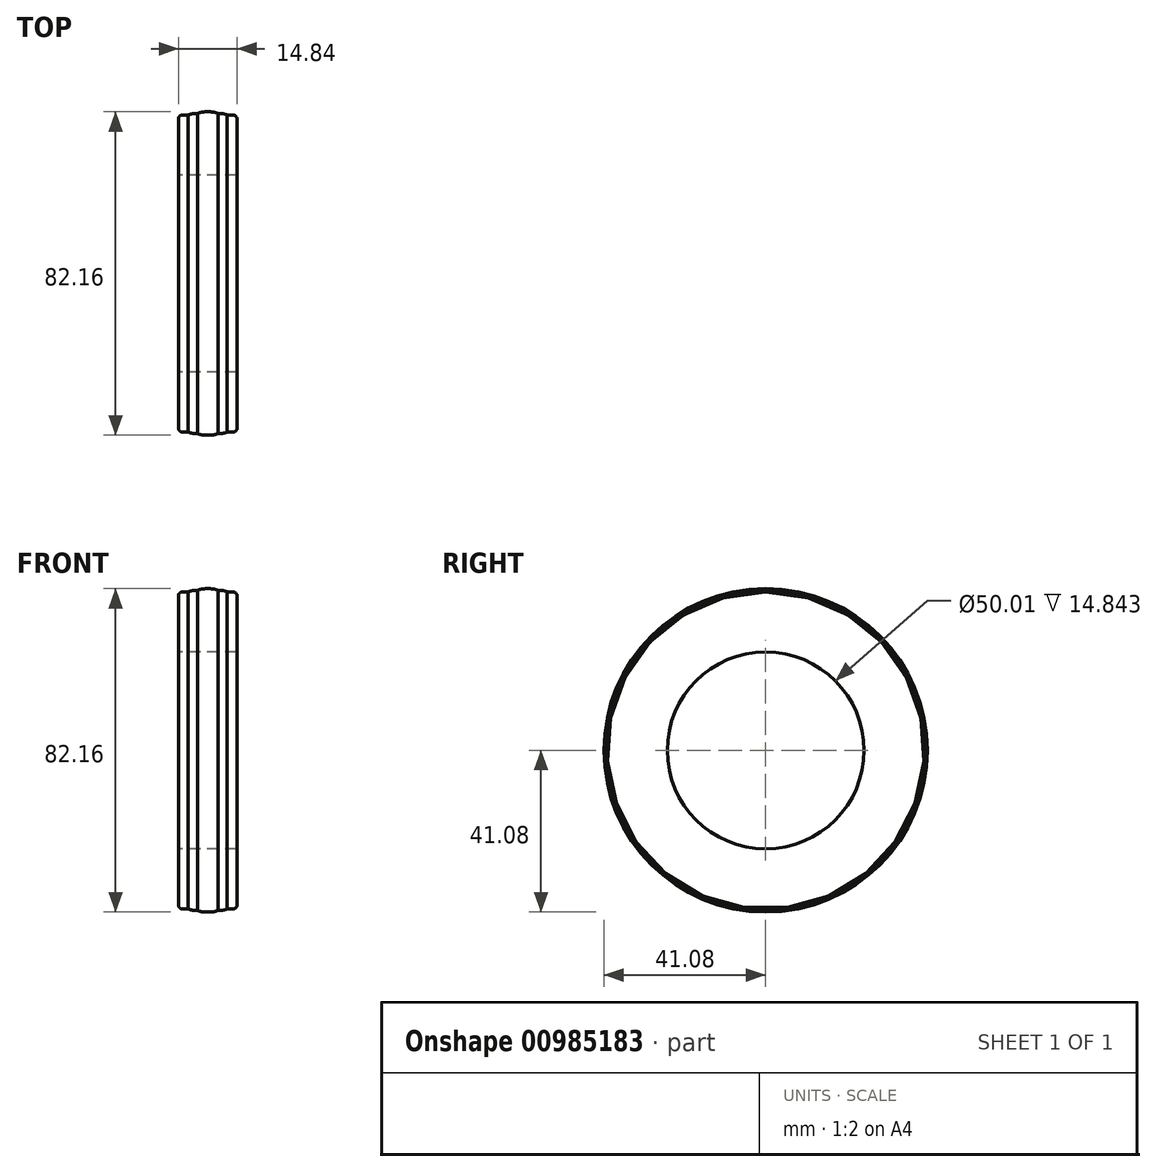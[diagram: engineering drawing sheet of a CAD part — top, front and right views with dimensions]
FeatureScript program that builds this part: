
annotation { "Feature Type Name" : "Feature", "Feature Type Description" : "" }
export const myFeature = defineFeature(function(context is Context, id is Id, definition is map)
    precondition{}
    {
        {
            var Q0;
            Q0=qCreatedBy(makeId("Front.planeOp"),FACE);
            var sketch = newSketch(context, id + "F0", { "sketchPlane" : qUnion([Q0])});
            skLineSegment(sketch, "E0", {"start": v(-55.67, 0) * mm, "end": v(68.03, 0) * mm, "construction": true});
            skLineSegment(sketch, "E1", {"start": v(-7.42, 0) * mm, "end": v(-7.42, 40.28) * mm});
            skLineSegment(sketch, "E2", {"start": v(-7.42, 40.28) * mm, "end": v(-4.96, 40.28) * mm});
            skLineSegment(sketch, "E3", {"start": v(-4.96, 40.28) * mm, "end": v(-4.96, 40.68) * mm});
            skLineSegment(sketch, "E4", {"start": v(-4.96, 40.68) * mm, "end": v(-2.58, 40.68) * mm});
            skLineSegment(sketch, "E5", {"start": v(-2.58, 40.68) * mm, "end": v(-2.58, 41.08) * mm});
            skLineSegment(sketch, "E6", {"start": v(-2.58, 41.08) * mm, "end": v(2.58, 41.08) * mm});
            skLineSegment(sketch, "E7", {"start": v(2.58, 41.08) * mm, "end": v(2.58, 40.68) * mm});
            skLineSegment(sketch, "E8", {"start": v(2.58, 40.68) * mm, "end": v(4.96, 40.68) * mm});
            skLineSegment(sketch, "E9", {"start": v(4.96, 40.68) * mm, "end": v(4.96, 40.28) * mm});
            skLineSegment(sketch, "E10", {"start": v(4.96, 40.28) * mm, "end": v(7.42, 40.28) * mm});
            skLineSegment(sketch, "E11", {"start": v(7.42, 40.28) * mm, "end": v(7.42, 0) * mm});
            skLineSegment(sketch, "E12", {"start": v(7.42, 0) * mm, "end": v(-7.42, 0) * mm});
            skLineSegment(sketch, "E13", {"start": v(0, 0) * mm, "end": v(0, 47.43) * mm, "construction": true});
            skSolve(sketch);
        }
        {
            var Q0;
            Q0=makeQuery(id+"F0.imprint","IMPRINT",FACE,{"disambiguationData":[TD([[makeQuery(id+"F0.imprint","IMPRINT",EDGE,{"derivedFrom":sQuery(id+"F0.wireOp",EDGE,"E1")}),-1.0]])]});
            var Q1;
            Q1=sQuery(id+"F0.wireOp",EDGE,"E0");
            revolve(context, id + "F1", {"surfaceOperationType" : NewSurfaceOperationType.NEW, "entities" : qUnion([Q0]), "axis" : qUnion([Q1]), "revolveType" : RevolveType.FULL});
        }
        {
            var Q0;
            Q0=makeQuery(id+"F1.opRevolve","SWEPT_EDGE",EDGE,{"disambiguationData":[OSD([sQuery(id+"F0.wireOp",EDGE,"E10"),sQuery(id+"F0.wireOp",EDGE,"E11")])]});
            var Q1;
            Q1=makeQuery(id+"F1.opRevolve","SWEPT_EDGE",EDGE,{"disambiguationData":[OSD([sQuery(id+"F0.wireOp",EDGE,"E1"),sQuery(id+"F0.wireOp",EDGE,"E2")])]});
            fillet(context, id + "F2", {"entities" : qUnion([Q0, Q1]), "radius" : 0.76 * mm, "tangentPropagation" : true, "rho" : 0.2, "crossSection" : FilletCrossSection.CONIC, "allowEdgeOverflow" : false});
        }
        {
            var Q0;
            Q0=makeQuery(id+"F1.opRevolve","SWEPT_EDGE",EDGE,{"disambiguationData":[OSD([sQuery(id+"F0.wireOp",EDGE,"E8"),sQuery(id+"F0.wireOp",EDGE,"E9")])]});
            var Q1;
            Q1=makeQuery(id+"F1.opRevolve","SWEPT_EDGE",EDGE,{"disambiguationData":[OSD([sQuery(id+"F0.wireOp",EDGE,"E3"),sQuery(id+"F0.wireOp",EDGE,"E4")])]});
            fillet(context, id + "F3", {"entities" : qUnion([Q0, Q1]), "radius" : 5.08 * mm, "tangentPropagation" : true, "allowEdgeOverflow" : false});
        }
        {
            var Q0;
            Q0=makeQuery(id+"F1.opRevolve","SWEPT_EDGE",EDGE,{"disambiguationData":[OSD([sQuery(id+"F0.wireOp",EDGE,"E6"),sQuery(id+"F0.wireOp",EDGE,"E7")])]});
            var Q1;
            Q1=makeQuery(id+"F1.opRevolve","SWEPT_EDGE",EDGE,{"disambiguationData":[OSD([sQuery(id+"F0.wireOp",EDGE,"E5"),sQuery(id+"F0.wireOp",EDGE,"E6")])]});
            fillet(context, id + "F4", {"entities" : qUnion([Q0, Q1]), "radius" : 5.08 * mm, "tangentPropagation" : true, "allowEdgeOverflow" : false});
        }
        {
            var Q0;
            Q0=qCreatedBy(makeId("Right.planeOp"),FACE);
            var sketch = newSketch(context, id + "F5", { "sketchPlane" : qUnion([Q0])});
            skCircle(sketch, "E14", {"center": v(0, 0) * mm, "radius": 25 * mm});
            skSolve(sketch);
        }
        {
            var Q0;
            Q0=qSketchRegion(id+"F5",true);
            extrude(context, id + "F6", {"entities" : qUnion([Q0]), "operationType" : NewBodyOperationType.REMOVE, "endBound" : BoundingType.THROUGH_ALL, "depth" : 25.4 * mm, "offsetDistance" : 25.4 * mm, "hasSecondDirection" : true, "secondDirectionBound" : SecondDirectionBoundingType.THROUGH_ALL, "secondDirectionOppositeDirection" : true, "secondDirectionDepth" : 25.4 * mm});
        }
    });
